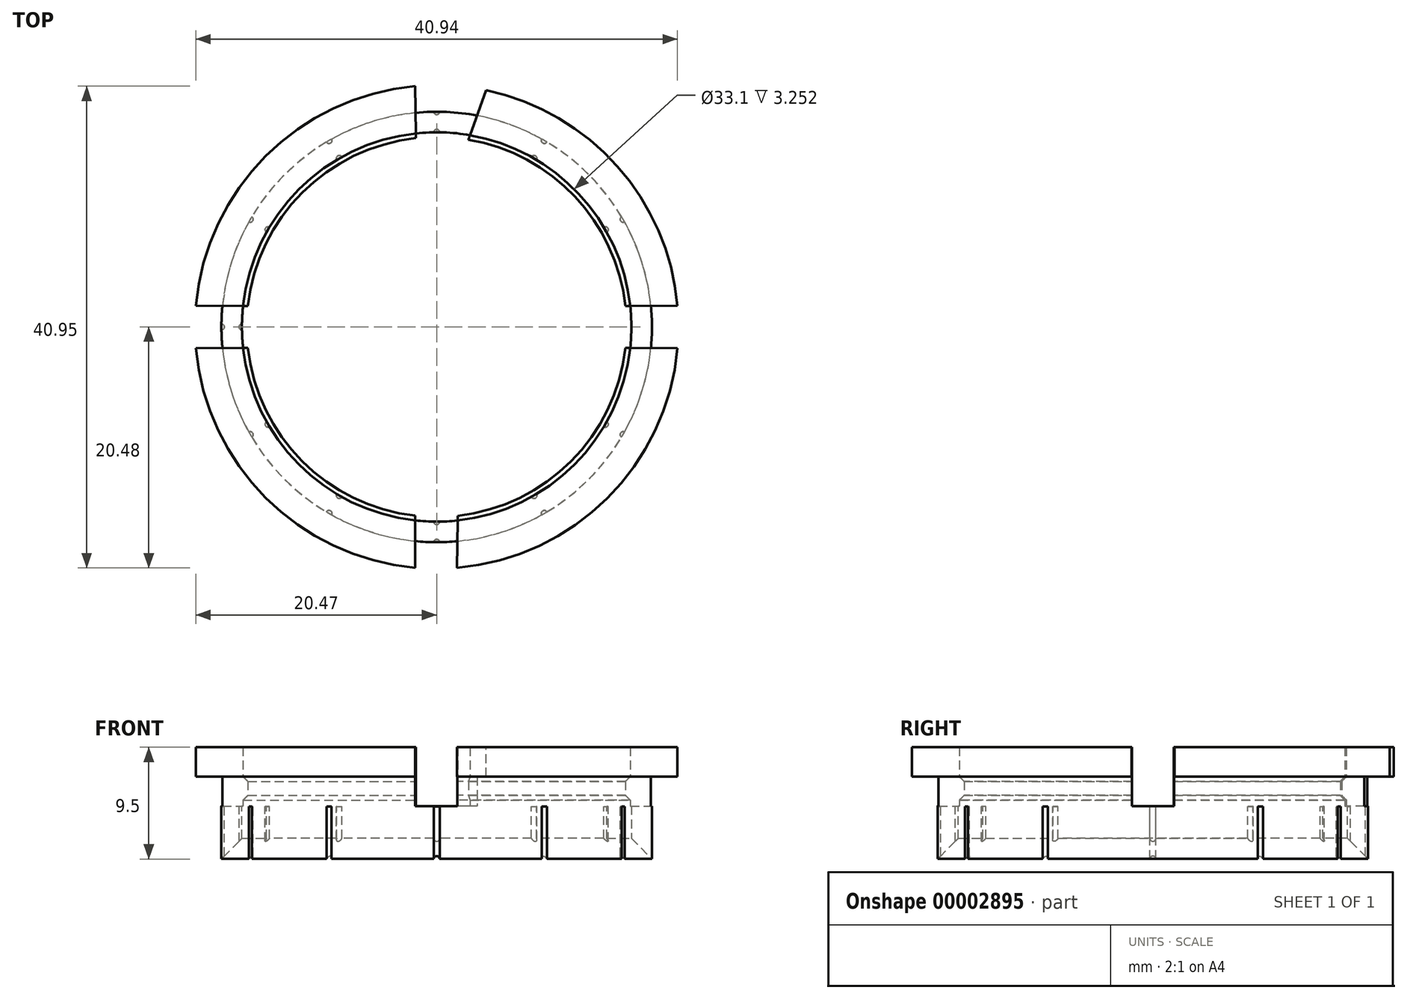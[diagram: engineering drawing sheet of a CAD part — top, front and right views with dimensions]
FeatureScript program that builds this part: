
annotation { "Feature Type Name" : "Feature", "Feature Type Description" : "" }
export const myFeature = defineFeature(function(context is Context, id is Id, definition is map)
    precondition{}
    {
        {
            var Q0;
            Q0=qCreatedBy(makeId("Right.planeOp"),FACE);
            var sketch = newSketch(context, id + "F0", { "sketchPlane" : qUnion([Q0])});
            skLineSegment(sketch, "E0", {"start": v(-20.55, 5.02) * mm, "end": v(-16.55, 5.02) * mm});
            skLineSegment(sketch, "E1", {"start": v(-16.55, 5.02) * mm, "end": v(-16.55, 2.52) * mm});
            skLineSegment(sketch, "E2", {"start": v(-16.55, 2.52) * mm, "end": v(-16.15, 2.12) * mm});
            skLineSegment(sketch, "E3", {"start": v(-16.15, 2.12) * mm, "end": v(-16.15, 0.92) * mm});
            skLineSegment(sketch, "E4", {"start": v(-16.15, 0.92) * mm, "end": v(-16.55, 0.52) * mm});
            skLineSegment(sketch, "E5", {"start": v(-16.55, 0.52) * mm, "end": v(-16.55, -2.73) * mm});
            skLineSegment(sketch, "E6", {"start": v(-16.55, -2.73) * mm, "end": v(-18.3, -4.48) * mm});
            skLineSegment(sketch, "E7", {"start": v(-18.3, -4.48) * mm, "end": v(-18.3, 2.52) * mm});
            skLineSegment(sketch, "E8", {"start": v(-18.3, 2.52) * mm, "end": v(-20.55, 2.52) * mm});
            skLineSegment(sketch, "E9", {"start": v(-20.55, 2.52) * mm, "end": v(-20.55, 5.02) * mm});
            skLineSegment(sketch, "E10", {"start": v(0, 0) * mm, "end": v(0, 10.1) * mm, "construction": true});
            skSolve(sketch);
        }
        {
            var Q0;
            Q0=makeQuery(id+"F0.imprint","IMPRINT",FACE,{"disambiguationData":[TD([[makeQuery(id+"F0.imprint","IMPRINT",EDGE,{"derivedFrom":sQuery(id+"F0.wireOp",EDGE,"E0")}),-1.0]])]});
            var Q1;
            Q1=sQuery(id+"F0.wireOp",EDGE,"E10");
            revolve(context, id + "F1", {"entities" : qUnion([Q0]), "axis" : qUnion([Q1]), "revolveType" : RevolveType.FULL});
        }
        {
            var Q0;
            Q0=makeQuery(id+"F1.opRevolve","SWEPT_FACE",FACE,{"disambiguationData":[OSD([sQuery(id+"F0.wireOp",EDGE,"E0")])]});
            var sketch = newSketch(context, id + "F2", { "sketchPlane" : qUnion([Q0])});
            skLineSegment(sketch, "E11", {"start": v(-20.55, 0) * mm, "end": v(-18.55, 0) * mm, "construction": true});
            skLineSegment(sketch, "E12", {"start": v(0, -20.55) * mm, "end": v(0, -18.55) * mm, "construction": true});
            skLineSegment(sketch, "E13.0", {"start": v(-1.82, -20.56) * mm, "end": v(-1.82, -16.45) * mm, "construction": true});
            skArc(sketch, "E14.0.0", {"start": v(-1.82, -20.47) * mm, "mid": v(-0.05, -20.55) * mm, "end": v(1.73, -20.48) * mm, "construction": true});
            skLineSegment(sketch, "E15.trimOffspring", {"start": v(2.2, 20.23) * mm, "end": v(2.2, 20.43) * mm, "construction": true});
            skLineSegment(sketch, "E16.trimOffspring", {"start": v(16.46, 1.78) * mm, "end": v(20.47, 1.82) * mm, "construction": true});
            skLineSegment(sketch, "E17.trimOffspring", {"start": v(16.55, 0) * mm, "end": v(20.55, 0) * mm, "construction": true});
            skLineSegment(sketch, "E18.trimOffspring", {"start": v(16.46, -1.78) * mm, "end": v(20.47, -1.82) * mm, "construction": true});
            skArc(sketch, "E19.trimOffspring", {"start": v(-20.47, 1.82) * mm, "mid": v(-20.54, 0) * mm, "end": v(-20.47, -1.82) * mm, "construction": true});
            skArc(sketch, "E20.trimOffspring", {"start": v(-20.47, 1.82) * mm, "mid": v(-20.55, 0) * mm, "end": v(-20.47, -1.82) * mm, "construction": true});
            skArc(sketch, "E21.trimOffspring", {"start": v(-1.82, -16.45) * mm, "mid": v(20.4, -1.33) * mm, "end": v(4.2, 20.11) * mm, "construction": true});
            skArc(sketch, "E22.trimOffspring", {"start": v(4.2, 20.11) * mm, "mid": v(3.2, 20.2) * mm, "end": v(2.2, 20.23) * mm, "construction": true});
            skArc(sketch, "E23.trimOffspring", {"start": v(4.2, 20.12) * mm, "mid": v(1.2, 20.51) * mm, "end": v(-1.82, 20.47) * mm, "construction": true});
            skLineSegment(sketch, "E24", {"start": v(-20.47, -1.82) * mm, "end": v(-13.24, -1.74) * mm});
            skLineSegment(sketch, "E25", {"start": v(-20.47, 1.82) * mm, "end": v(-13.24, 1.74) * mm});
            skLineSegment(sketch, "E26", {"start": v(-1.82, 20.47) * mm, "end": v(-1.74, 13.24) * mm});
            skLineSegment(sketch, "E27", {"start": v(4.2, 20.12) * mm, "end": v(1.74, 13.24) * mm});
            skLineSegment(sketch, "E28", {"start": v(-1.82, -20.47) * mm, "end": v(-1.82, -13.23) * mm});
            skLineSegment(sketch, "E29", {"start": v(1.73, -20.48) * mm, "end": v(1.81, -13.23) * mm});
            skLineSegment(sketch, "E30", {"start": v(13.24, -1.74) * mm, "end": v(20.47, -1.82) * mm});
            skLineSegment(sketch, "E31", {"start": v(13.24, 1.74) * mm, "end": v(20.47, 1.82) * mm});
            skArc(sketch, "E32.0", {"start": v(-20.47, 1.82) * mm, "mid": v(-20.55, 0) * mm, "end": v(-20.47, -1.82) * mm});
            skArc(sketch, "E33.trimOffspring", {"start": v(-1.82, -20.47) * mm, "mid": v(-0.05, -20.55) * mm, "end": v(1.73, -20.48) * mm});
            skArc(sketch, "E34.trimOffspring", {"start": v(20.47, -1.82) * mm, "mid": v(20.55, 0) * mm, "end": v(20.47, 1.82) * mm});
            skArc(sketch, "E35.trimOffspring", {"start": v(4.2, 20.12) * mm, "mid": v(1.2, 20.51) * mm, "end": v(-1.82, 20.47) * mm});
            skArc(sketch, "E36.trimOffspring", {"start": v(20.47, -1.82) * mm, "mid": v(20.55, 0) * mm, "end": v(20.47, 1.82) * mm, "construction": true});
            skArc(sketch, "E37", {"start": v(1.74, 13.24) * mm, "mid": v(0, 13.35) * mm, "end": v(-1.74, 13.24) * mm});
            skArc(sketch, "E38.trimOffspring", {"start": v(-13.24, 1.74) * mm, "mid": v(-13.35, 0) * mm, "end": v(-13.24, -1.74) * mm});
            skArc(sketch, "E39.trimOffspring", {"start": v(-1.82, -13.23) * mm, "mid": v(0, -13.35) * mm, "end": v(1.81, -13.23) * mm});
            skArc(sketch, "E40.trimOffspring", {"start": v(13.24, -1.74) * mm, "mid": v(13.35, 0) * mm, "end": v(13.24, 1.74) * mm});
            skArc(sketch, "E41.trimOffspring", {"start": v(2.2, 20.23) * mm, "mid": v(-10.95, 14.87) * mm, "end": v(-16.46, 1.78) * mm, "construction": true});
            skSolve(sketch);
        }
        {
            var Q0;
            Q0 = qSketchRegion(id + "F2", true);
            var Q1;
            {var subQ2=sQuery(id+"F2.wireOp",EDGE,"E26");Q1=makeQuery(id+"F2.imprint","IMPRINT",FACE,{"disambiguationData":[TD([[makeQuery(id+"F2.imprint","IMPRINT",EDGE,{"derivedFrom":subQ2}),1.0]])]});}
            var Q2;
            {var subQ2=sQuery(id+"F2.wireOp",EDGE,"E24");Q2=makeQuery(id+"F2.imprint","IMPRINT",FACE,{"disambiguationData":[TD([[makeQuery(id+"F2.imprint","IMPRINT",EDGE,{"derivedFrom":subQ2}),1.0]])]});}
            var Q3;
            {var subQ2=sQuery(id+"F2.wireOp",EDGE,"E30");Q3=makeQuery(id+"F2.imprint","IMPRINT",FACE,{"disambiguationData":[TD([[makeQuery(id+"F2.imprint","IMPRINT",EDGE,{"derivedFrom":subQ2}),1.0]])]});}
            var Q4;
            {var subQ2=sQuery(id+"F2.wireOp",EDGE,"E28");Q4=makeQuery(id+"F2.imprint","IMPRINT",FACE,{"disambiguationData":[TD([[makeQuery(id+"F2.imprint","IMPRINT",EDGE,{"derivedFrom":subQ2}),-1.0]])]});}
            extrude(context, id + "F3", {"entities" : qUnion([Q0, Q1, Q2, Q3, Q4]), "operationType" : NewBodyOperationType.REMOVE, "oppositeDirection" : true, "depth" : 5 * mm});
        }
        {
            var Q0;
            Q0=qCreatedBy(makeId("Top.planeOp"),FACE);
            var sketch = newSketch(context, id + "F4", { "sketchPlane" : qUnion([Q0])});
            skCircle(sketch, "E42.0", {"center": v(0, 0) * mm, "radius": 16.55 * mm, "construction": true});
            skCircle(sketch, "E43", {"center": v(14.33, -8.27) * mm, "radius": 0.25 * mm});
            skCircle(sketch, "E44", {"center": v(8.28, -14.33) * mm, "radius": 0.25 * mm});
            skCircle(sketch, "E45", {"center": v(-8.27, -14.33) * mm, "radius": 0.25 * mm});
            skCircle(sketch, "E46", {"center": v(0, -16.55) * mm, "radius": 0.25 * mm});
            skCircle(sketch, "E47", {"center": v(-14.33, -8.28) * mm, "radius": 0.25 * mm});
            skLineSegment(sketch, "E48", {"start": v(0, 0) * mm, "end": v(16.8, 0) * mm, "construction": true});
            skLineSegment(sketch, "E49", {"start": v(0, 0) * mm, "end": v(15.85, -9.15) * mm, "construction": true});
            skLineSegment(sketch, "E50", {"start": v(0, 0) * mm, "end": v(9.15, -15.85) * mm, "construction": true});
            skLineSegment(sketch, "E51", {"start": v(0, 0) * mm, "end": v(-9.15, -15.85) * mm, "construction": true});
            skLineSegment(sketch, "E52", {"start": v(0, 0) * mm, "end": v(0, -18.3) * mm, "construction": true});
            skLineSegment(sketch, "E53", {"start": v(0, 0) * mm, "end": v(-15.85, -9.15) * mm, "construction": true});
            skLineSegment(sketch, "E54", {"start": v(-18.3, 0) * mm, "end": v(0, 0) * mm, "construction": true});
            skCircle(sketch, "E55.0.MirrorC", {"center": v(14.33, 8.27) * mm, "radius": 0.25 * mm});
            skCircle(sketch, "E56.0.MirrorC", {"center": v(8.28, 14.33) * mm, "radius": 0.25 * mm});
            skCircle(sketch, "E57.0.MirrorC", {"center": v(0, 16.55) * mm, "radius": 0.25 * mm});
            skCircle(sketch, "E58.0.MirrorC", {"center": v(-8.27, 14.33) * mm, "radius": 0.25 * mm});
            skCircle(sketch, "E59.0.MirrorC", {"center": v(-14.33, 8.28) * mm, "radius": 0.25 * mm});
            skCircle(sketch, "E60.0.MirrorC", {"center": v(-16.55, 0) * mm, "radius": 0.25 * mm});
            skCircle(sketch, "E61", {"center": v(-18.3, 0) * mm, "radius": 0.25 * mm});
            skCircle(sketch, "E62", {"center": v(-15.85, -9.15) * mm, "radius": 0.25 * mm});
            skCircle(sketch, "E63", {"center": v(-9.15, -15.85) * mm, "radius": 0.25 * mm});
            skCircle(sketch, "E64", {"center": v(9.15, -15.85) * mm, "radius": 0.25 * mm});
            skCircle(sketch, "E65", {"center": v(15.85, -9.15) * mm, "radius": 0.25 * mm});
            skCircle(sketch, "E66", {"center": v(0, -18.3) * mm, "radius": 0.25 * mm});
            skCircle(sketch, "E67.0.MirrorC", {"center": v(-15.85, 9.15) * mm, "radius": 0.25 * mm});
            skCircle(sketch, "E68.0.MirrorC", {"center": v(-9.15, 15.85) * mm, "radius": 0.25 * mm});
            skCircle(sketch, "E69.0.MirrorC", {"center": v(0, 18.3) * mm, "radius": 0.25 * mm});
            skCircle(sketch, "E70.0.MirrorC", {"center": v(9.15, 15.85) * mm, "radius": 0.25 * mm});
            skCircle(sketch, "E71.0.MirrorC", {"center": v(15.85, 9.15) * mm, "radius": 0.25 * mm});
            skSolve(sketch);
        }
        {
            var Q0;
            Q0 = qSketchRegion(id + "F4", true);
            extrude(context, id + "F5", {"entities" : qUnion([Q0]), "operationType" : NewBodyOperationType.REMOVE, "oppositeDirection" : true, "depth" : 25 * mm});
        }
    });
